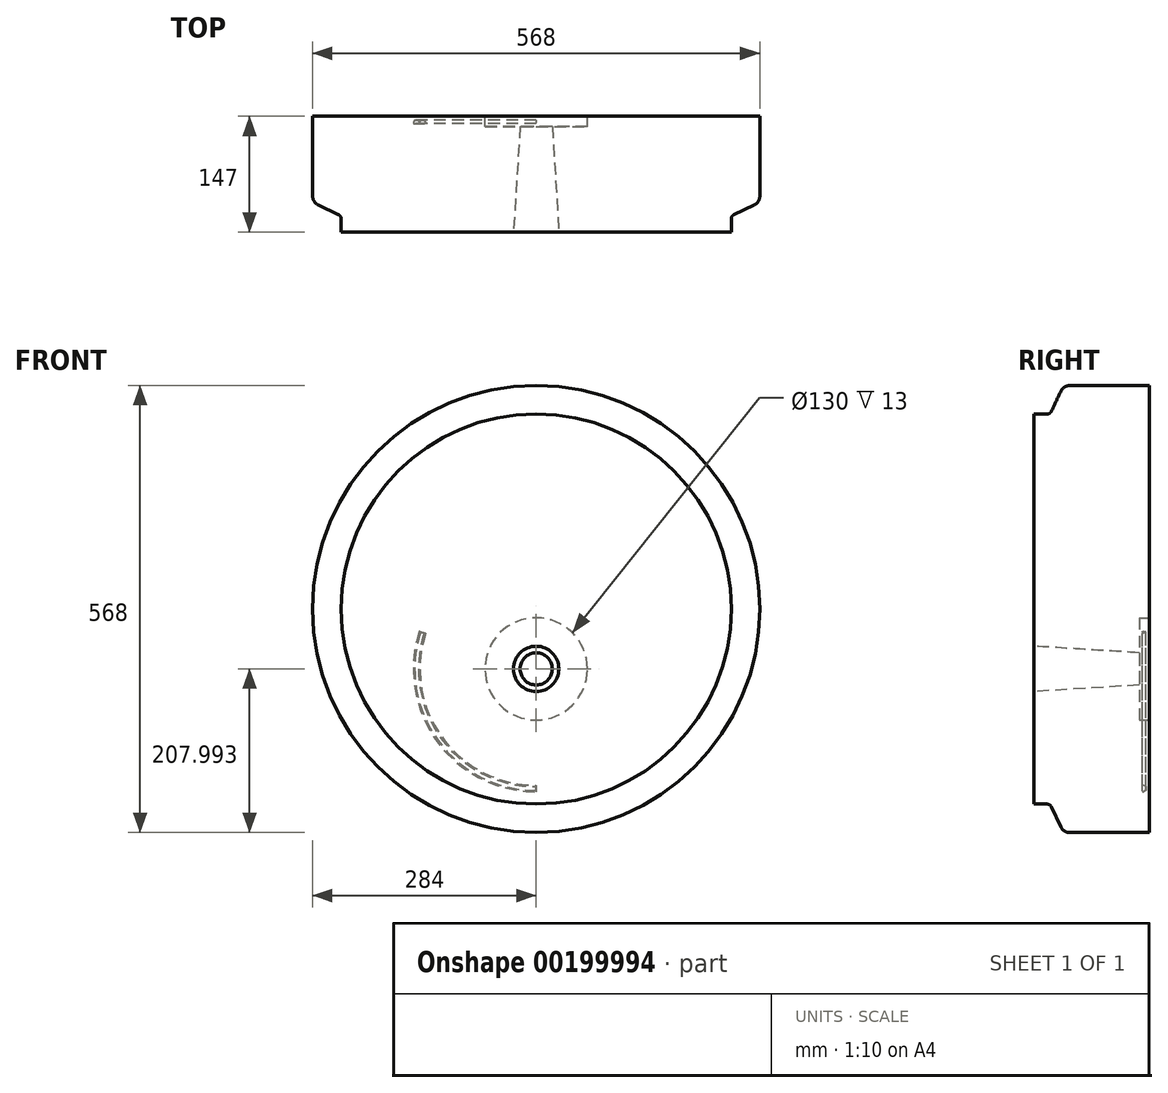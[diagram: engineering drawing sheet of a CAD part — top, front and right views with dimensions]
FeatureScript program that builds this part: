
annotation { "Feature Type Name" : "Feature", "Feature Type Description" : "" }
export const myFeature = defineFeature(function(context is Context, id is Id, definition is map)
    precondition{}
    {
        {
            var Q0;
            Q0=qCreatedBy(makeId("Front.planeOp"),FACE);
            var sketch = newSketch(context, id + "F0", { "sketchPlane" : qUnion([Q0])});
            skCircle(sketch, "E0", {"center": v(0, 0) * mm, "radius": 284 * mm});
            skSolve(sketch);
        }
        {
            var Q0;
            Q0 = qSketchRegion(id + "F0", true);
            extrude(context, id + "F1", {"entities" : qUnion([Q0]), "depth" : 147 * mm});
        }
        {
            var Q0;
            Q0=makeQuery(id+"F1.opExtrude","CAP_FACE",FACE,{"disambiguationData":[OSD([sQuery(id+"F0.wireOp",EDGE,"E0")])],"isStart":false});
            var sketch = newSketch(context, id + "F2", { "sketchPlane" : qUnion([Q0])});
            skPoint(sketch, "E1", {"position": v(0, -76) * mm});
            skSolve(sketch);
        }
        {
            var Q0;
            Q0=sQuery(id+"F2.wireOp",VERTEX,"E1");
            var Q1;
            Q1=makeQuery(id+"F1.opExtrude","SWEPT_BODY",BODY,{"disambiguationData":[OSD([sQuery(id+"F0.wireOp",EDGE,"E0")])]});
            hole(context, id + "F3", {"style" : HoleStyle.SIMPLE, "endStyle" : HoleEndStyle.THROUGH, "holeDiameter" : 40 * mm, "startFromSketch" : true, "locations" : qUnion([Q0]), "scope" : qUnion([Q1]), "isTappedThrough" : true});
        }
        {
            var Q0;
            Q0=makeQuery(id+"F1.opExtrude","CAP_FACE",FACE,{"disambiguationData":[OSD([sQuery(id+"F0.wireOp",EDGE,"E0")])],"isStart":false});
            var sketch = newSketch(context, id + "F4", { "sketchPlane" : qUnion([Q0])});
            skCircle(sketch, "E2", {"center": v(0, -76) * mm, "radius": 28.82 * mm});
            skSolve(sketch);
        }
        {
            var Q0;
            Q0 = qSketchRegion(id + "F4", true);
            extrude(context, id + "F5", {"entities" : qUnion([Q0]), "operationType" : NewBodyOperationType.REMOVE, "oppositeDirection" : true, "depth" : 200 * mm, "hasDraft" : true, "draftAngle" : 3.58 * degree, "draftPullDirection" : true});
        }
        {
            var Q0;
            Q0=makeQuery(id+"F1.opExtrude","CAP_FACE",FACE,{"disambiguationData":[OSD([sQuery(id+"F0.wireOp",EDGE,"E0")])],"isStart":true});
            var sketch = newSketch(context, id + "F6", { "sketchPlane" : qUnion([Q0])});
            skCircle(sketch, "E3", {"center": v(0, -76) * mm, "radius": 20 * mm});
            skSolve(sketch);
        }
        {
            var Q0;
            Q0=makeQuery(id+"F6.imprint","IMPRINT",FACE,{"disambiguationData":[TD([[makeQuery(id+"F6.imprint","IMPRINT",EDGE,{"derivedFrom":sQuery(id+"F6.wireOp",EDGE,"E3")}),-1.0]])]});
            var sketch = newSketch(context, id + "F7", { "sketchPlane" : qUnion([Q0])});
            skCircle(sketch, "E4", {"center": v(0, -76) * mm, "radius": 65 * mm});
            skSolve(sketch);
        }
        {
            var Q0;
            Q0 = qSketchRegion(id + "F7", true);
            extrude(context, id + "F8", {"entities" : qUnion([Q0]), "operationType" : NewBodyOperationType.REMOVE, "oppositeDirection" : true, "depth" : 13 * mm});
        }
        {
            var Q0;
            Q0=qCreatedBy(makeId("Right.planeOp"),FACE);
            var sketch = newSketch(context, id + "F9", { "sketchPlane" : qUnion([Q0])});
            skLineSegment(sketch, "E5", {"start": v(0, 0) * mm, "end": v(-207.82, 0) * mm});
            skLineSegment(sketch, "E6", {"start": v(-103, 297.86) * mm, "end": v(-166.74, 297.86) * mm});
            skLineSegment(sketch, "E7", {"start": v(-166.74, 297.86) * mm, "end": v(-150.46, 257.22) * mm});
            skLineSegment(sketch, "E8", {"start": v(0, 275.97) * mm, "end": v(0, 306.84) * mm});
            skLineSegment(sketch, "E9.0", {"start": v(-116.54, 257.22) * mm, "end": v(-116.54, 268.8) * mm});
            skLineSegment(sketch, "E10", {"start": v(-124.6, 251.5) * mm, "end": v(-103, 297.86) * mm});
            skLineSegment(sketch, "E11", {"start": v(-163.39, 247.8) * mm, "end": v(-130.4, 247.8) * mm});
            skArc(sketch, "E12.filletArc", {"start": v(-130.4, 247.8) * mm, "mid": v(-126.97, 248.8) * mm, "end": v(-124.6, 251.5) * mm});
            skLineSegment(sketch, "E13", {"start": v(-150.46, 257.22) * mm, "end": v(-163.39, 246.72) * mm});
            skSolve(sketch);
        }
        {
            var Q0;
            Q0 = qSketchRegion(id + "F9", true);
            var Q1;
            Q1=sQuery(id+"F9.wireOp",EDGE,"E5");
            revolve(context, id + "F10", {"operationType" : NewBodyOperationType.REMOVE, "entities" : qUnion([Q0]), "axis" : qUnion([Q1]), "revolveType" : RevolveType.FULL});
        }
        {
            var Q0;
            Q0=makeQuery(id+"F10.boolean.opBoolean","INTERSECT",EDGE,{"derivedFrom":[makeQuery(id+"F1.opExtrude","SWEPT_FACE",FACE,{"disambiguationData":[OSD([sQuery(id+"F0.wireOp",EDGE,"E0")])]}),makeQuery(id+"F10.opRevolve","SWEPT_FACE",FACE,{"disambiguationData":[OSD([sQuery(id+"F9.wireOp",EDGE,"E10")])]})]});
            fillet(context, id + "F11", {"entities" : qUnion([Q0]), "radius" : 13 * mm, "tangentPropagation" : true, "allowEdgeOverflow" : false});
        }
        {
            var Q0;
            Q0=makeQuery(id+"F6.imprint","IMPRINT",FACE,{"disambiguationData":[TD([[makeQuery(id+"F6.imprint","IMPRINT",EDGE,{"derivedFrom":sQuery(id+"F6.wireOp",EDGE,"E3")}),-1.0]])]});
            var sketch = newSketch(context, id + "F12", { "sketchPlane" : qUnion([Q0])});
            skArc(sketch, "E14", {"start": v(0, -228.1) * mm, "mid": v(122.75, -165.76) * mm, "end": v(144.8, -29.86) * mm});
            skLineSegment(sketch, "E15", {"start": v(0, 171.9) * mm, "end": v(33.8, 171.9) * mm});
            skArc(sketch, "E16", {"start": v(99.8, 120.99) * mm, "mid": v(75.47, 157.69) * mm, "end": v(33.8, 171.9) * mm});
            skLineSegment(sketch, "E17", {"start": v(98.51, 125.3) * mm, "end": v(144.8, -29.86) * mm});
            skPoint(sketch, "E18.end.orphan", {"position": v(33.8, 106.9) * mm});
            skArc(sketch, "E19.MirrorCS", {"start": v(-99.8, 120.99) * mm, "mid": v(-75.47, 157.69) * mm, "end": v(-33.8, 171.9) * mm});
            skLineSegment(sketch, "E20.MirrorCS", {"start": v(0, 171.9) * mm, "end": v(-33.8, 171.9) * mm});
            skLineSegment(sketch, "E21.MirrorCS", {"start": v(-98.51, 125.3) * mm, "end": v(-144.8, -29.86) * mm});
            skArc(sketch, "E22.MirrorCS", {"start": v(0, -228.1) * mm, "mid": v(-122.75, -165.76) * mm, "end": v(-144.8, -29.86) * mm});
            skPoint(sketch, "E23.orphan", {"position": v(52.15, 171.9) * mm});
            skPoint(sketch, "E24.orphan", {"position": v(-52.15, 171.9) * mm});
            skSolve(sketch);
        }
        {
            var Q0;
            Q0=qCreatedBy(makeId("Right.planeOp"),FACE);
            var sketch = newSketch(context, id + "F13", { "sketchPlane" : qUnion([Q0])});
            skLineSegment(sketch, "E25", {"start": v(-4.6, -225.55) * mm, "end": v(-4.6, -230.45) * mm});
            skPoint(sketch, "E26.end.orphan", {"position": v(22.61, -228) * mm});
            skArc(sketch, "E27.MirrorCS", {"start": v(-9.2, -231.27) * mm, "mid": v(-8.84, -231.94) * mm, "end": v(-8.07, -232) * mm});
            skArc(sketch, "E28.MirrorCS", {"start": v(-9.2, -224.73) * mm, "mid": v(-8.84, -224.06) * mm, "end": v(-8.07, -224) * mm});
            skPoint(sketch, "E29.MirrorP", {"position": v(-9.2, -232.5) * mm});
            skLineSegment(sketch, "E30.MirrorCS", {"start": v(-9.2, -228.22) * mm, "end": v(-9.2, -224.73) * mm});
            skLineSegment(sketch, "E31.MirrorCS", {"start": v(-4.6, -225.55) * mm, "end": v(-8.07, -224) * mm});
            skLineSegment(sketch, "E32.MirrorCS", {"start": v(-9.2, -227.78) * mm, "end": v(-9.2, -231.27) * mm});
            skLineSegment(sketch, "E33.MirrorCS", {"start": v(-4.6, -230.45) * mm, "end": v(-8.07, -232) * mm});
            skPoint(sketch, "E34", {"position": v(-4.6, -232.5) * mm});
            skSolve(sketch);
        }
        {
            var Q0;
            Q0 = qSketchRegion(id + "F13", true);
            var Q1;
            Q1=sQuery(id+"F12.wireOp",EDGE,"E14");
            sweep(context, id + "F14", {"operationType" : NewBodyOperationType.REMOVE, "profiles" : qUnion([Q0]), "path" : qUnion([Q1])});
        }
    });
